# Revit family: Faucet_Touchless-Lavatory-KOHLER-Oblo-K-103BB76_1
name_source: partatom
category: Plumbing Fixtures
units: mm (PartAtom-declared; Revit-internal decimal feet)

## family parameters
Cut with Voids When Loaded = No
Host = Face
OmniClass Number = 23.31.11.00
OmniClass Title = Faucets
Part Type = Normal
Room Calculation Point = No
Round Connector Dimension = Use Diameter
Shared = No

## types (4) — shared parameters
ADA Compliant = No
Apparent Load = 0 VA
Assembly Code = D2010
CW Connection = Yes
Cold Water Inlet = Cold Water Inlet
Date Modified = 05/14/2023
Default Elevation = 36"
Description = BASIC-AC-NO DRAIN/ NO MIXER
Drain Included = No
Electrical Connector = Yes
Electrical Note = One Dedicated Circuit Required
Faucet Hole Spacing = 0"
Flow Rate = 1 GPM
HW Connection = Yes
Handle Clearance = 0"
Height = 8 1/16"
Hot Water Inlet = Hot Water Inlet
Length = 5 1/4"
Manufacturer = Kohler Co.
Master Format 2014 = 22 41 39
Master Format 2014 Name = Residential Faucets, Supplies, and Trim
Material = Premium Metal Construction
Pressure = 0.00 psi
Product Documentation Link = https://www.us.kohler.com
Product Name = Oblo
Product Page URL = http://www.us.kohler.com
Spout Reach = 5 1/4"
URL = https://www.us.kohler.com
Vent Connection = No
Voltage = 220 V
Waste Connection = No
Waste Water Outlet = Waste Water Outlet
WaterSense Certified = No
Width = 2 5/16"

## per-type parameters (varying)
| type | Finish | Model | Type |
| 2MB-Vibrant Brushed Moderne Brass | Kohler-Metal-2MB-Vibrant_Brushed_Moderne_Brass | K-103BB76-SBNA-2MB | 1 |
| BL-Matte Black | Kohler-Metal-BL-Matte_Black | K-103BB76-SBNA-BL | 2 |
| BN-Vibrant Brushed Nickel | Kohler-Metal-BN-Vibrant_Brushed_Nickel | K-103BB76-SBNA-BN | 3 |
| CP-Polished Chrome | Kohler-Metal-CP-Polished_Chrome | K-103BB76-SBNA-CP | 4 |

## geometry (parser evidence)
native form markers: Sweep x4
no freeform markers — native parametric forms only
